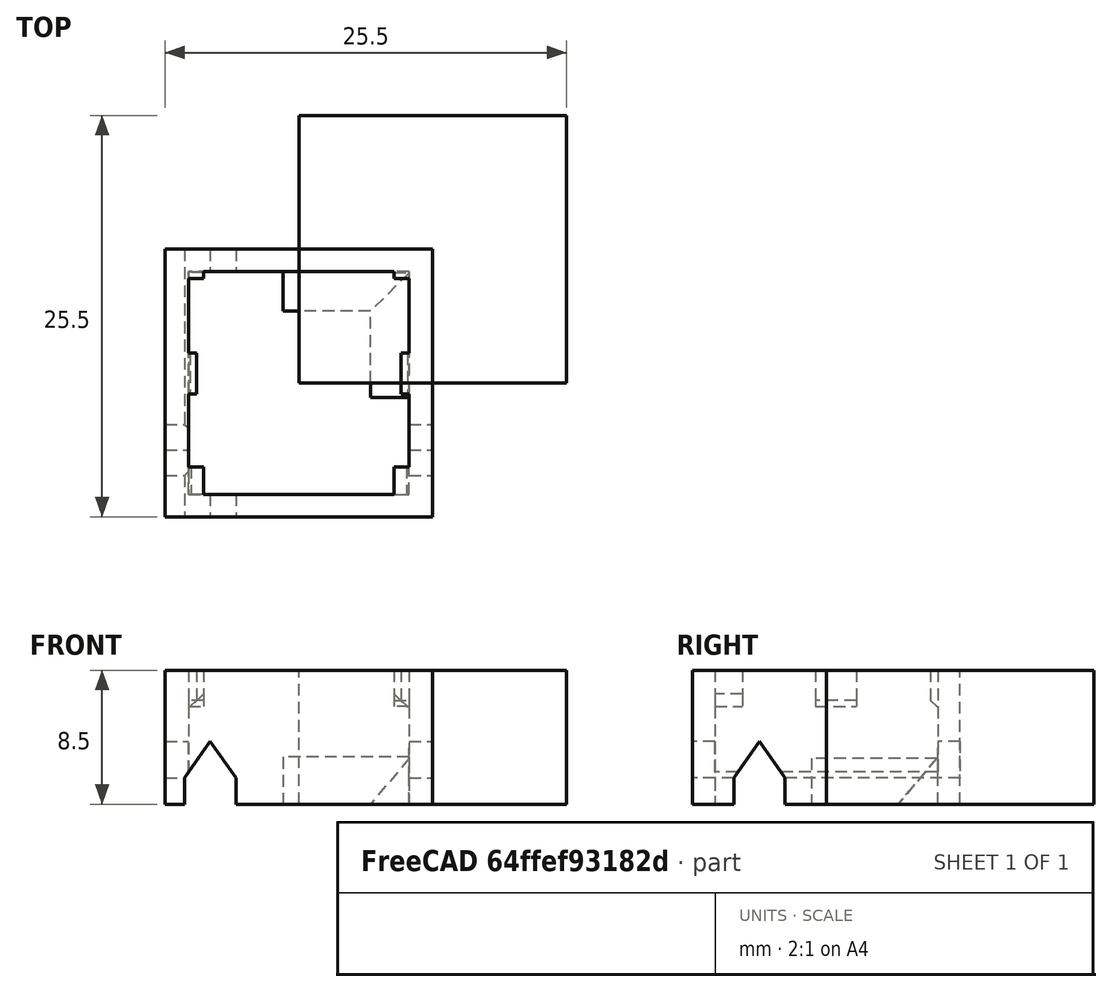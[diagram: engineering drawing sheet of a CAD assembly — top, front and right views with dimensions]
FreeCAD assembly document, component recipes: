
FREECAD ASSEMBLY — COMPONENT RECIPES ("milli-ergo-drafting")

This assembly document has 2 components, labeled P0..P1 below (a component is one placed body or linked part). 1 of them carries a construction recipe — the FreeCAD feature program that regenerates the part from scratch, quoted from this document or its linked companion documents; the rest are supplied as boundary geometry only. No exploded tour is included for this assembly.
COMPONENT P0 — recipe-attached ("Body", modeled in this document).
Construction recipe (the document's own serialized feature program — sketch geometry with constraints, then the solid features built on it; lengths are millimeters unless a unit is written):

FEATURE [PartDesign::AdditiveBox] Box
  AttacherType = Attacher::AttachEngine3D
  Height = 8.5
  Length = 17
  Refine = true
  Suppressed = false
  Width = 17
  expr: Height = <<ref>>.z
  expr: Length = <<ref>>.x
  expr: Width = <<ref>>.y
FEATURE [Sketcher::SketchObject] Sketch
  ArcFitTolerance = 1e-06
  AttachmentSupport = -> [Box]
  ExternalGeometry = -> [Box]
  FullyConstrained = false
  MakeInternals = false
  MapMode = 5
  Placement = pos=(0,0,8.5) rot=(0,0,1;0rad)
  sketch-geometry (12):
    g0: LineSegment [constr] StartX=0 StartY=17 StartZ=0 EndX=0 EndY=0 EndZ=0
    g1: LineSegment [constr] StartX=0 StartY=0 StartZ=0 EndX=17 EndY=0 EndZ=0
    g2: LineSegment [constr] StartX=17 StartY=0 StartZ=0 EndX=17 EndY=17 EndZ=0
    g3: LineSegment [constr] StartX=17 StartY=17 StartZ=0 EndX=0 EndY=17 EndZ=0
    g4: LineSegment StartX=15.5 StartY=15.5 StartZ=0 EndX=1.5 EndY=15.5 EndZ=0
    g5: LineSegment StartX=1.5 StartY=15.5 StartZ=0 EndX=1.5 EndY=1.5 EndZ=0
    g6: LineSegment StartX=1.5 StartY=1.5 StartZ=0 EndX=15.5 EndY=1.5 EndZ=0
    g7: LineSegment StartX=15.5 StartY=1.5 StartZ=0 EndX=15.5 EndY=15.5 EndZ=0
    g8: LineSegment [constr] StartX=12.5 StartY=15.5 StartZ=0 EndX=12.5 EndY=17 EndZ=0
    g9: LineSegment [constr] StartX=1.5 StartY=12.4999 StartZ=0 EndX=0 EndY=12.4999 EndZ=0
    g10: LineSegment [constr] StartX=1.5 StartY=1.5 StartZ=0 EndX=1.5 EndY=0 EndZ=0
    g11: LineSegment [constr] StartX=15.5 StartY=1.50013 StartZ=0 EndX=17 EndY=1.50013 EndZ=0
  constraints (34):
    c: Coincident(g0,g1)
    c: Coincident(g1,g2)
    c: Coincident(g2,g3)
    c: Coincident(g3,g0)
    c: Vertical(g0)
    c: Vertical(g2)
    c: Horizontal(g1)
    c: Horizontal(g3)
    c: Coincident(g0,g-5)
    c: Coincident(g1,g-6)
    c: Coincident(g4,g5)
    c: Coincident(g4,g7)
    c: Coincident(g5,g6)
    c: Coincident(g6,g7)
    c: Perpendicular(g8,g4)
    c: PointOnObject(g8,g4)
    c: PointOnObject(g8,g3)
    c: Perpendicular(g9,g5)
    c: PointOnObject(g9,g5)
    c: PointOnObject(g9,g0)
    c: Perpendicular(g10,g6)
    c: PointOnObject(g10,g6)
    c: PointOnObject(g10,g1)
    c: Perpendicular(g11,g7)
    c: PointOnObject(g11,g7)
    c: PointOnObject(g11,g2)
    c: Parallel(g7,g2)
    c: Parallel(g4,g3)
    c: Parallel(g5,g0)
    c: Equal(g9,g8)
    c: Parallel(g6,g1)
    c: Equal(g10,g8)
    c: Equal(g11,g8)
    c: Distance(g8) = 1.5
FEATURE [PartDesign::Body] Body
  AllowCompound = false
  Group = -> [Box,Sketch]
  Origin = -> Origin
  Tip = -> Box
COMPONENT P1 — geometry summary ("keymount"; no construction recipe available for this part):
  bounding box: 17.0 x 17.0 x 8.5 mm
  tessellated surface: 228 triangles
  volume: 780 mm^3 (32% of its bounding box)
PROVENANCE & LICENSES
A FreeCAD (.FCStd) document from a public repository crawl; recipes are the document's own serialized feature recipes (and, for linked parts, companion documents' recipes).
License: as declared in the source repository (recorded in the dataset sidecar).
